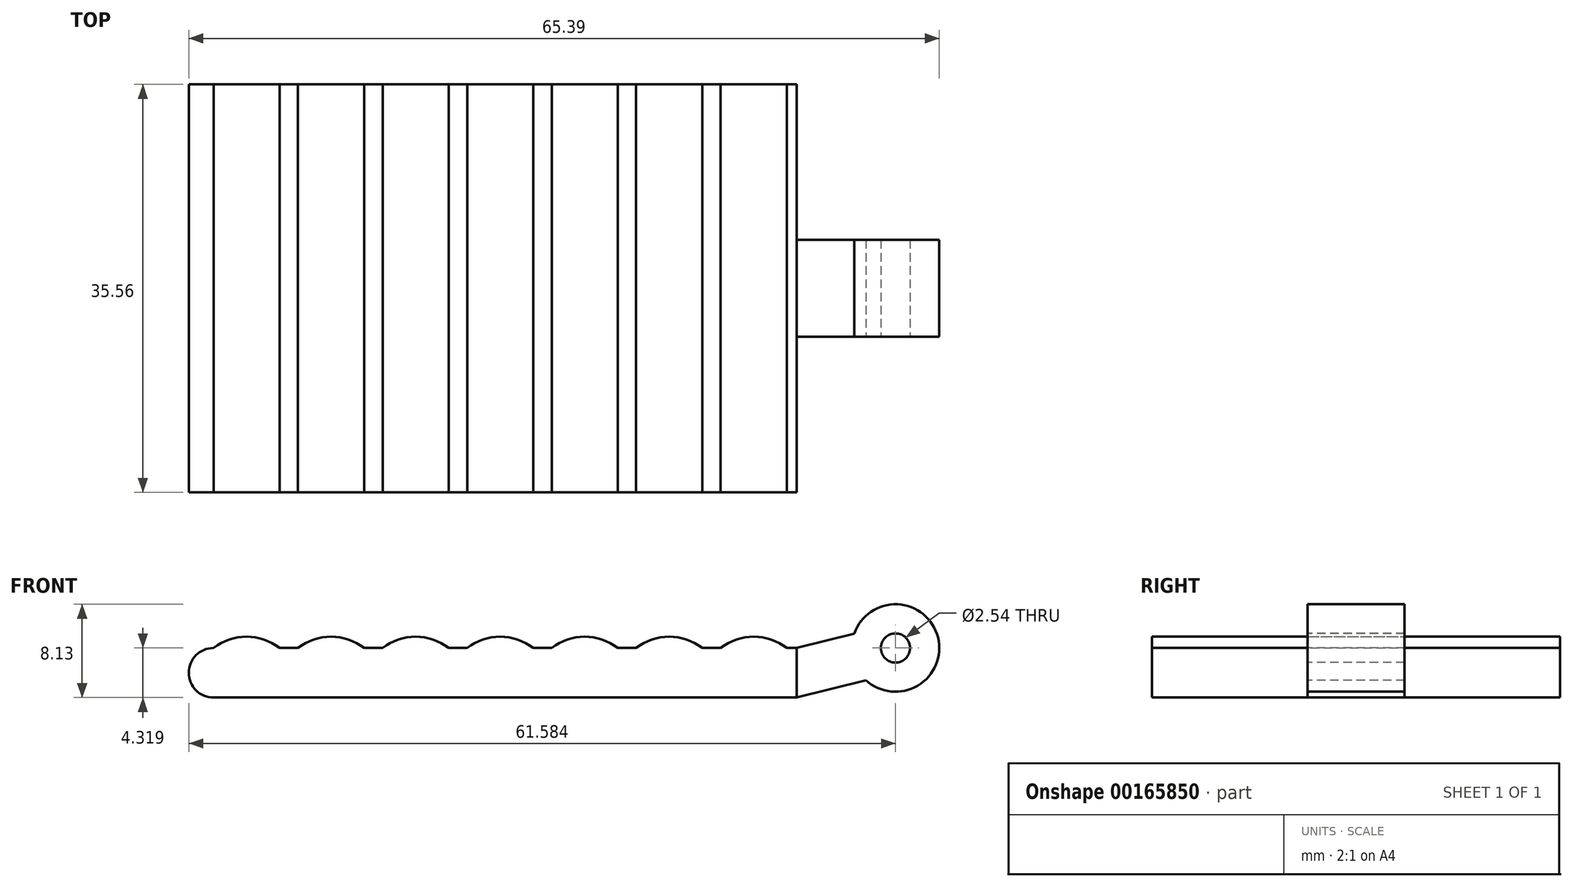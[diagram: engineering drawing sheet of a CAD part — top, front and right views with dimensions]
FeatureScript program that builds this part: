
annotation { "Feature Type Name" : "Feature", "Feature Type Description" : "" }
export const myFeature = defineFeature(function(context is Context, id is Id, definition is map)
    precondition{}
    {
        {
            var Q0;
            Q0=qCreatedBy(makeId("Front.planeOp"),FACE);
            var sketch = newSketch(context, id + "F0", { "sketchPlane" : qUnion([Q0])});
            skLineSegment(sketch, "E0.bottom", {"start": v(25.4, -2.16) * mm, "end": v(-25.4, -2.16) * mm});
            skLineSegment(sketch, "E0.top", {"start": v(25.4, 2.16) * mm, "end": v(-25.4, 2.16) * mm});
            skLineSegment(sketch, "E0.left", {"start": v(25.4, -2.16) * mm, "end": v(25.4, 2.16) * mm});
            skLineSegment(sketch, "E0.right", {"start": v(-25.4, -2.16) * mm, "end": v(-25.4, 2.16) * mm});
            skPoint(sketch, "E0.middle", {"position": v(0, 0) * mm});
            skLineSegment(sketch, "E1", {"start": v(25.4, 2.16) * mm, "end": v(34.02, 4.32) * mm});
            skLineSegment(sketch, "E2", {"start": v(25.4, -2.16) * mm, "end": v(34.02, 0) * mm});
            skLineSegment(sketch, "E3", {"start": v(34.02, 4.32) * mm, "end": v(34.02, 0) * mm});
            skPoint(sketch, "E4", {"position": v(34.02, 2.16) * mm});
            skCircle(sketch, "E5", {"center": v(34.02, 2.16) * mm, "radius": 3.81 * mm});
            skArc(sketch, "E6", {"start": v(-25.4, 2.16) * mm, "mid": v(-27.56, 0) * mm, "end": v(-25.4, -2.16) * mm});
            skArc(sketch, "E7", {"start": v(-19.65, 2.16) * mm, "mid": v(-22.53, 3.14) * mm, "end": v(-25.4, 2.16) * mm});
            skArc(sketch, "E8.1.0.0", {"start": v(-12.28, 2.16) * mm, "mid": v(-15.16, 3.14) * mm, "end": v(-18.03, 2.16) * mm});
            skArc(sketch, "E8.2.0.0", {"start": v(-4.92, 2.16) * mm, "mid": v(-7.8, 3.14) * mm, "end": v(-10.67, 2.16) * mm});
            skArc(sketch, "E8.3.0.0", {"start": v(2.45, 2.16) * mm, "mid": v(-0.43, 3.14) * mm, "end": v(-3.3, 2.16) * mm});
            skArc(sketch, "E8.4.0.0", {"start": v(9.81, 2.16) * mm, "mid": v(6.94, 3.14) * mm, "end": v(4.06, 2.16) * mm});
            skArc(sketch, "E8.5.0.0", {"start": v(17.18, 2.16) * mm, "mid": v(14.3, 3.14) * mm, "end": v(11.43, 2.16) * mm});
            skArc(sketch, "E8.6.0.0", {"start": v(24.55, 2.16) * mm, "mid": v(21.67, 3.14) * mm, "end": v(18.8, 2.16) * mm});
            skLineSegment(sketch, "E8.direction1", {"start": v(-22.53, -1.56) * mm, "end": v(-15.16, -1.56) * mm, "construction": true});
            skSolve(sketch);
        }
        {
            var Q0;
            Q0=makeQuery(id+"F0.imprint","IMPRINT",FACE,{"disambiguationData":[TD([[makeQuery(id+"F0.imprint","IMPRINT",EDGE,{"derivedFrom":sQuery(id+"F0.wireOp",EDGE,"E0.right")}),1.0]])]});
            var Q1;
            Q1=makeQuery(id+"F0.imprint","IMPRINT",FACE,{"disambiguationData":[TD([[makeQuery(id+"F0.imprint","IMPRINT",EDGE,{"derivedFrom":sQuery(id+"F0.wireOp",EDGE,"E0.bottom")}),-1.0]])]});
            extrude(context, id + "F1", {"entities" : qUnion([Q0, Q1]), "endBound" : BoundingType.SYMMETRIC, "depth" : 35.56 * mm});
        }
        {
            var Q0;
            {var subQ0=sQuery(id+"F0.wireOp",EDGE,"E0.left");Q0=makeQuery(id+"F0.imprint","IMPRINT",FACE,{"disambiguationData":[TD([[makeQuery(id+"F0.imprint","IMPRINT",EDGE,{"derivedFrom":subQ0}),-1.0]])]});}
            var Q1;
            {var subQ0=sQuery(id+"F0.wireOp",EDGE,"E3");Q1=makeQuery(id+"F0.imprint","IMPRINT",FACE,{"disambiguationData":[TD([[makeQuery(id+"F0.imprint","IMPRINT",EDGE,{"derivedFrom":subQ0}),-1.0]])]});}
            var Q2;
            {var subQ0=sQuery(id+"F0.wireOp",EDGE,"E3");Q2=makeQuery(id+"F0.imprint","IMPRINT",FACE,{"disambiguationData":[TD([[makeQuery(id+"F0.imprint","IMPRINT",EDGE,{"derivedFrom":subQ0}),1.0]])]});}
            extrude(context, id + "F2", {"entities" : qUnion([Q0, Q1, Q2]), "operationType" : NewBodyOperationType.ADD, "endBound" : BoundingType.SYMMETRIC, "oppositeDirection" : true, "depth" : 8.46 * mm});
        }
        {
            var Q0;
            Q0=sQuery(id+"F0.wireOp",VERTEX,"E4");
            var Q1;
            Q1=makeQuery(id+"F1.opExtrude","SWEPT_BODY",BODY,{"disambiguationData":[OSD([sQuery(id+"F0.wireOp",EDGE,"E0.bottom"),sQuery(id+"F0.wireOp",EDGE,"E0.top"),sQuery(id+"F0.wireOp",EDGE,"E0.left"),sQuery(id+"F0.wireOp",EDGE,"E6")])]});
            hole(context, id + "F3", {"style" : HoleStyle.SIMPLE, "endStyle" : HoleEndStyle.THROUGH, "holeDiameter" : 2.54 * mm, "startFromSketch" : true, "locations" : qUnion([Q0]), "scope" : qUnion([Q1]), "isTappedThrough" : true});
        }
        {
            var Q0;
            Q0=sQuery(id+"F0.wireOp",VERTEX,"E4");
            var Q1;
            Q1=makeQuery(id+"F1.opExtrude","SWEPT_BODY",BODY,{"disambiguationData":[OSD([sQuery(id+"F0.wireOp",EDGE,"E0.bottom"),sQuery(id+"F0.wireOp",EDGE,"E0.top"),sQuery(id+"F0.wireOp",EDGE,"E0.left"),sQuery(id+"F0.wireOp",EDGE,"E6")])]});
            hole(context, id + "F4", {"style" : HoleStyle.SIMPLE, "endStyle" : HoleEndStyle.THROUGH, "oppositeDirection" : true, "holeDiameter" : 2.54 * mm, "startFromSketch" : true, "locations" : qUnion([Q0]), "scope" : qUnion([Q1]), "isTappedThrough" : true});
        }
        {
            var Q0;
            {var subQ0=sQuery(id+"F0.wireOp",EDGE,"E7");Q0=makeQuery(id+"F0.imprint","IMPRINT",FACE,{"disambiguationData":[TD([[makeQuery(id+"F0.imprint","IMPRINT",EDGE,{"derivedFrom":subQ0}),1.0]])]});}
            var Q1;
            {var subQ0=sQuery(id+"F0.wireOp",EDGE,"E8.1.0.0");Q1=makeQuery(id+"F0.imprint","IMPRINT",FACE,{"disambiguationData":[TD([[makeQuery(id+"F0.imprint","IMPRINT",EDGE,{"derivedFrom":subQ0}),1.0]])]});}
            var Q2;
            {var subQ0=sQuery(id+"F0.wireOp",EDGE,"E8.2.0.0");Q2=makeQuery(id+"F0.imprint","IMPRINT",FACE,{"disambiguationData":[TD([[makeQuery(id+"F0.imprint","IMPRINT",EDGE,{"derivedFrom":subQ0}),1.0]])]});}
            var Q3;
            {var subQ0=sQuery(id+"F0.wireOp",EDGE,"E8.3.0.0");Q3=makeQuery(id+"F0.imprint","IMPRINT",FACE,{"disambiguationData":[TD([[makeQuery(id+"F0.imprint","IMPRINT",EDGE,{"derivedFrom":subQ0}),1.0]])]});}
            var Q4;
            {var subQ0=sQuery(id+"F0.wireOp",EDGE,"E8.4.0.0");Q4=makeQuery(id+"F0.imprint","IMPRINT",FACE,{"disambiguationData":[TD([[makeQuery(id+"F0.imprint","IMPRINT",EDGE,{"derivedFrom":subQ0}),1.0]])]});}
            var Q5;
            {var subQ0=sQuery(id+"F0.wireOp",EDGE,"E8.5.0.0");Q5=makeQuery(id+"F0.imprint","IMPRINT",FACE,{"disambiguationData":[TD([[makeQuery(id+"F0.imprint","IMPRINT",EDGE,{"derivedFrom":subQ0}),1.0]])]});}
            var Q6;
            {var subQ0=sQuery(id+"F0.wireOp",EDGE,"E8.6.0.0");Q6=makeQuery(id+"F0.imprint","IMPRINT",FACE,{"disambiguationData":[TD([[makeQuery(id+"F0.imprint","IMPRINT",EDGE,{"derivedFrom":subQ0}),1.0]])]});}
            var Q7;
            Q7=makeQuery(id+"F1.opExtrude","CAP_FACE",FACE,{"disambiguationData":[OSD([sQuery(id+"F0.wireOp",EDGE,"E0.bottom"),sQuery(id+"F0.wireOp",EDGE,"E0.top"),sQuery(id+"F0.wireOp",EDGE,"E0.left"),sQuery(id+"F0.wireOp",EDGE,"E6")])],"isStart":true});
            var Q8;
            Q8=makeQuery(id+"F1.opExtrude","SWEPT_BODY",BODY,{"disambiguationData":[OSD([sQuery(id+"F0.wireOp",EDGE,"E0.bottom"),sQuery(id+"F0.wireOp",EDGE,"E0.top"),sQuery(id+"F0.wireOp",EDGE,"E0.left"),sQuery(id+"F0.wireOp",EDGE,"E6")])]});
            extrude(context, id + "F5", {"entities" : qUnion([Q0, Q1, Q2, Q3, Q4, Q5, Q6]), "operationType" : NewBodyOperationType.ADD, "endBound" : BoundingType.SYMMETRIC, "endBoundEntityFace" : qUnion([Q7]), "endBoundEntityBody" : qUnion([Q8]), "depth" : 35.56 * mm});
        }
    });
